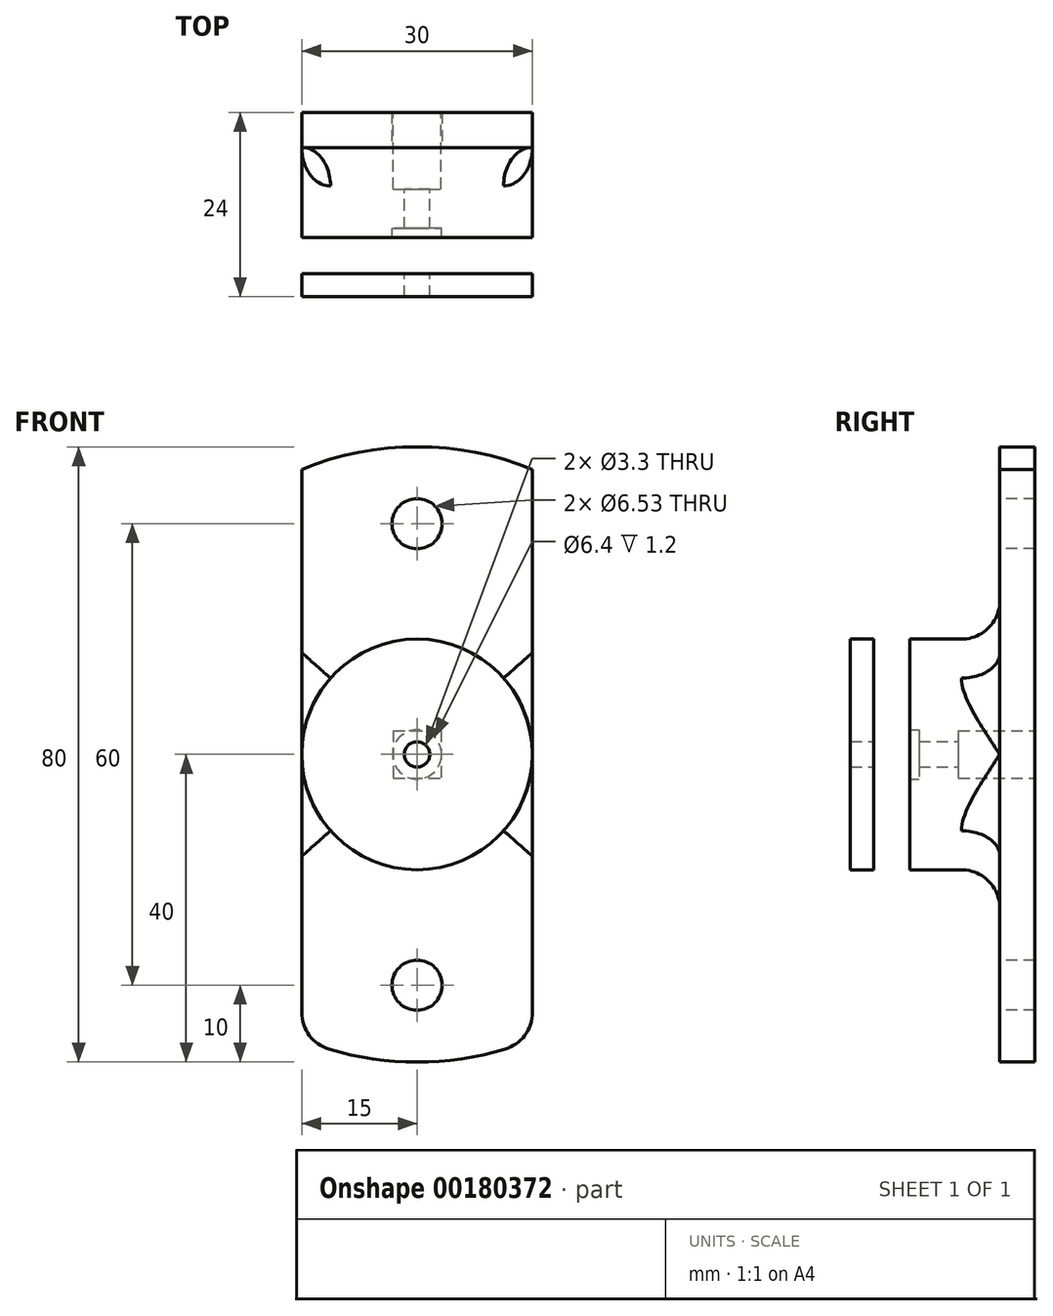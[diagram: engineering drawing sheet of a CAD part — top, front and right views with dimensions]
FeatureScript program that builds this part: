
annotation { "Feature Type Name" : "Feature", "Feature Type Description" : "" }
export const myFeature = defineFeature(function(context is Context, id is Id, definition is map)
    precondition{}
    {
        {
            var Q0;
            Q0=qCreatedBy(makeId("Right.planeOp"),FACE);
            var sketch = newSketch(context, id + "F0", { "sketchPlane" : qUnion([Q0])});
            skLineSegment(sketch, "E0", {"start": v(0, 0) * mm, "end": v(0, 15) * mm, "construction": true});
            skLineSegment(sketch, "E1", {"start": v(0, 15) * mm, "end": v(11.73, 15) * mm});
            skLineSegment(sketch, "E2", {"start": v(11.73, 15) * mm, "end": v(11.73, 40) * mm});
            skLineSegment(sketch, "E3", {"start": v(11.73, 40) * mm, "end": v(16.3, 40) * mm});
            skLineSegment(sketch, "E4", {"start": v(16.3, 40) * mm, "end": v(16.3, 0) * mm, "construction": true});
            skLineSegment(sketch, "E5", {"start": v(16.3, 0) * mm, "end": v(0, 0) * mm, "construction": true});
            skLineSegment(sketch, "E6", {"start": v(16.3, 40) * mm, "end": v(16.3, 3.1) * mm});
            skLineSegment(sketch, "E7", {"start": v(16.3, 3.1) * mm, "end": v(6.3, 3.1) * mm});
            skLineSegment(sketch, "E8", {"start": v(6.3, 3.1) * mm, "end": v(6.3, 1.65) * mm});
            skLineSegment(sketch, "E9", {"start": v(0, 1.65) * mm, "end": v(-7.7, 1.65) * mm, "construction": true});
            skLineSegment(sketch, "E10", {"start": v(6.3, 1.65) * mm, "end": v(1.2, 1.65) * mm});
            skLineSegment(sketch, "E11", {"start": v(1.2, 1.65) * mm, "end": v(1.2, 3.2) * mm});
            skLineSegment(sketch, "E12", {"start": v(1.2, 3.2) * mm, "end": v(0, 3.2) * mm});
            skLineSegment(sketch, "E13", {"start": v(0, 3.2) * mm, "end": v(0, 15) * mm});
            skLineSegment(sketch, "E14", {"start": v(-4.7, 1.65) * mm, "end": v(-4.7, 15) * mm});
            skLineSegment(sketch, "E15", {"start": v(-4.7, 15) * mm, "end": v(-7.7, 15) * mm});
            skLineSegment(sketch, "E16", {"start": v(-7.7, 15) * mm, "end": v(-7.7, 1.65) * mm});
            skLineSegment(sketch, "E17", {"start": v(-7.7, 1.65) * mm, "end": v(-4.7, 1.65) * mm});
            skSolve(sketch);
        }
        {
            var Q0;
            Q0=makeQuery(id+"F0.imprint","IMPRINT",FACE,{"disambiguationData":[TD([[makeQuery(id+"F0.imprint","IMPRINT",EDGE,{"derivedFrom":sQuery(id+"F0.wireOp",EDGE,"E1")}),-1.0]])]});
            var Q1;
            Q1 = qConstructionFilter(qBodyType(qCreatedBy(id + "F0" ,EDGE), BodyType.WIRE), ConstructionObject.NO);
            var Q2;
            Q2=sQuery(id+"F0.wireOp",EDGE,"E5");
            revolve(context, id + "F1", {"entities" : qUnion([Q0]), "surfaceEntities" : qUnion([Q1]), "axis" : qUnion([Q2]), "revolveType" : RevolveType.FULL});
        }
        {
            var Q0;
            Q0=makeQuery(id+"F0.imprint","IMPRINT",FACE,{"disambiguationData":[TD([[makeQuery(id+"F0.imprint","IMPRINT",EDGE,{"derivedFrom":sQuery(id+"F0.wireOp",EDGE,"E14")}),1.0]])]});
            var Q1;
            Q1=sQuery(id+"F0.wireOp",EDGE,"E5");
            revolve(context, id + "F2", {"entities" : qUnion([Q0]), "axis" : qUnion([Q1]), "revolveType" : RevolveType.FULL});
        }
        {
            var Q0;
            Q0=makeQuery(id+"F1.opRevolve","SWEPT_FACE",FACE,{"disambiguationData":[OSD([sQuery(id+"F0.wireOp",EDGE,"E2")])]});
            var sketch = newSketch(context, id + "F3", { "sketchPlane" : qUnion([Q0])});
            skLineSegment(sketch, "E18", {"start": v(0, 0) * mm, "end": v(0, 40) * mm, "construction": true});
            skLineSegment(sketch, "E19", {"start": v(15, 0) * mm, "end": v(15, 41.17) * mm});
            skLineSegment(sketch, "E20", {"start": v(15, 41.17) * mm, "end": v(44.36, 41.17) * mm});
            skLineSegment(sketch, "E21", {"start": v(44.36, 41.17) * mm, "end": v(44.36, -53.09) * mm});
            skLineSegment(sketch, "E22", {"start": v(44.36, -53.09) * mm, "end": v(15, -53.09) * mm});
            skLineSegment(sketch, "E23", {"start": v(15, -53.09) * mm, "end": v(15, 0) * mm});
            skLineSegment(sketch, "E24.MirrorCS", {"start": v(-15, -53.09) * mm, "end": v(-15, 0) * mm});
            skLineSegment(sketch, "E25.MirrorCS", {"start": v(-44.36, -53.09) * mm, "end": v(-15, -53.09) * mm});
            skLineSegment(sketch, "E26.MirrorCS", {"start": v(-15, 41.17) * mm, "end": v(-44.36, 41.17) * mm});
            skLineSegment(sketch, "E27.MirrorCS", {"start": v(-44.36, 41.17) * mm, "end": v(-44.36, -53.09) * mm});
            skLineSegment(sketch, "E28.MirrorCS", {"start": v(-15, 0) * mm, "end": v(-15, 41.17) * mm});
            skSolve(sketch);
        }
        {
            var Q0;
            {var subQ1=sQuery(id+"F3.wireOp",EDGE,"E24.MirrorCS");var subQ2=sQuery(id+"F0.wireOp",EDGE,"E2");var subQ4=makeQuery(id+"F1.opRevolve","SWEPT_EDGE",EDGE,{"disambiguationData":[OSD([subQ2,sQuery(id+"F0.wireOp",EDGE,"E3")])]});var subQ5=makeQuery(id+"F3.imprint","INTERSECT",VERTEX,{"derivedFrom":[subQ4,subQ1]});Q0=makeQuery(id+"F3.imprint","IMPRINT",FACE,{"disambiguationData":[TD([[makeQuery(id+"F3.imprint","IMPRINT",EDGE,{"disambiguationData":[TD([[subQ5,-1.0]])],"derivedFrom":subQ1}),1.0]])]});}
            var Q1;
            {var subQ1=sQuery(id+"F3.wireOp",EDGE,"E19");var subQ2=sQuery(id+"F0.wireOp",EDGE,"E2");var subQ4=makeQuery(id+"F1.opRevolve","SWEPT_EDGE",EDGE,{"disambiguationData":[OSD([subQ2,sQuery(id+"F0.wireOp",EDGE,"E3")])]});var subQ5=makeQuery(id+"F3.imprint","INTERSECT",VERTEX,{"derivedFrom":[subQ4,subQ1]});Q1=makeQuery(id+"F3.imprint","IMPRINT",FACE,{"disambiguationData":[TD([[makeQuery(id+"F3.imprint","IMPRINT",EDGE,{"disambiguationData":[TD([[subQ5,1.0]])],"derivedFrom":subQ1}),-1.0]])]});}
            extrude(context, id + "F4", {"entities" : qUnion([Q0, Q1]), "operationType" : NewBodyOperationType.REMOVE, "oppositeDirection" : true, "depth" : 25 * mm});
        }
        {
            var Q0;
            Q0=makeQuery(id+"F4.boolean.opBoolean","COPY",EDGE,{"derivedFrom":makeQuery(id+"F4.opExtrude","SWEPT_EDGE",EDGE,{"disambiguationData":[OSD([sQuery(id+"F0.wireOp",EDGE,"E2"),sQuery(id+"F0.wireOp",EDGE,"E3"),sQuery(id+"F3.wireOp",EDGE,"E19")])]})});
            var Q1;
            Q1=makeQuery(id+"F4.boolean.opBoolean","COPY",EDGE,{"derivedFrom":makeQuery(id+"F4.opExtrude","SWEPT_EDGE",EDGE,{"disambiguationData":[OSD([sQuery(id+"F0.wireOp",EDGE,"E2"),sQuery(id+"F0.wireOp",EDGE,"E3"),sQuery(id+"F3.wireOp",EDGE,"E28.MirrorCS")])]})});
            var Q2;
            Q2=makeQuery(id+"F4.boolean.opBoolean","COPY",EDGE,{"derivedFrom":makeQuery(id+"F4.opExtrude","SWEPT_EDGE",EDGE,{"disambiguationData":[OSD([sQuery(id+"F0.wireOp",EDGE,"E2"),sQuery(id+"F0.wireOp",EDGE,"E3"),sQuery(id+"F3.wireOp",EDGE,"E23")])]})});
            var Q3;
            Q3=makeQuery(id+"F4.boolean.opBoolean","COPY",EDGE,{"derivedFrom":makeQuery(id+"F4.opExtrude","SWEPT_EDGE",EDGE,{"disambiguationData":[OSD([sQuery(id+"F0.wireOp",EDGE,"E2"),sQuery(id+"F0.wireOp",EDGE,"E3"),sQuery(id+"F3.wireOp",EDGE,"E24.MirrorCS")])]})});
            var Q4;
            Q4=makeQuery(id+"F4.boolean.opBoolean","SPLIT",EDGE,{"disambiguationData":[OD(1.0)],"derivedFrom":makeQuery(id+"F1.opRevolve","SWEPT_EDGE",EDGE,{"disambiguationData":[OSD([sQuery(id+"F0.wireOp",EDGE,"E1"),sQuery(id+"F0.wireOp",EDGE,"E2")])]})});
            fillet(context, id + "F5", {"entities" : qUnion([Q0, Q1, Q2, Q3, Q4]), "radius" : 5 * mm, "tangentPropagation" : true, "allowEdgeOverflow" : false});
        }
        {
            var Q0;
            Q0=makeQuery(id+"F4.boolean.opBoolean","SPLIT",FACE,{"disambiguationData":[OD(0.0)],"derivedFrom":makeQuery(id+"F1.opRevolve","SWEPT_FACE",FACE,{"disambiguationData":[OSD([sQuery(id+"F0.wireOp",EDGE,"E2")])]})});
            var sketch = newSketch(context, id + "F6", { "sketchPlane" : qUnion([Q0])});
            skLineSegment(sketch, "E29", {"start": v(0, 0) * mm, "end": v(-47.52, 0) * mm, "construction": true});
            skCircle(sketch, "E30", {"center": v(0, 30) * mm, "radius": 3.26 * mm});
            skLineSegment(sketch, "E31", {"start": v(0, 30) * mm, "end": v(0, 20) * mm, "construction": true});
            skLineSegment(sketch, "E32", {"start": v(0, 30) * mm, "end": v(0, 40) * mm, "construction": true});
            skCircle(sketch, "E33.MirrorC", {"center": v(0, -30) * mm, "radius": 3.26 * mm});
            skSolve(sketch);
        }
        {
            var Q0;
            Q0 = qSketchRegion(id + "F6", true);
            extrude(context, id + "F7", {"entities" : qUnion([Q0]), "operationType" : NewBodyOperationType.REMOVE, "endBound" : BoundingType.THROUGH_ALL, "oppositeDirection" : true, "depth" : 25 * mm});
        }
        {
            var Q0;
            Q0=makeQuery(id+"F1.opRevolve","SWEPT_FACE",FACE,{"disambiguationData":[OSD([sQuery(id+"F0.wireOp",EDGE,"E6")])]});
            var sketch = newSketch(context, id + "F8", { "sketchPlane" : qUnion([Q0])});
            skLineSegment(sketch, "E34.bottom", {"start": v(3.1, 3.1) * mm, "end": v(-3.1, 3.1) * mm});
            skLineSegment(sketch, "E34.top", {"start": v(3.1, -3.1) * mm, "end": v(-3.1, -3.1) * mm});
            skLineSegment(sketch, "E34.left", {"start": v(3.1, 3.1) * mm, "end": v(3.1, -3.1) * mm});
            skLineSegment(sketch, "E34.right", {"start": v(-3.1, 3.1) * mm, "end": v(-3.1, -3.1) * mm});
            skPoint(sketch, "E34.middle", {"position": v(0, 0) * mm});
            skSolve(sketch);
        }
        {
            var Q0;
            Q0 = qSketchRegion(id + "F8", true);
            var Q1;
            Q1=makeQuery(id+"F1.opRevolve","SWEPT_FACE",FACE,{"disambiguationData":[OSD([sQuery(id+"F0.wireOp",EDGE,"E8")])]});
            extrude(context, id + "F9", {"entities" : qUnion([Q0]), "operationType" : NewBodyOperationType.REMOVE, "endBound" : BoundingType.UP_TO_SURFACE, "oppositeDirection" : true, "endBoundEntityFace" : qUnion([Q1]), "depth" : 25 * mm});
        }
    });
